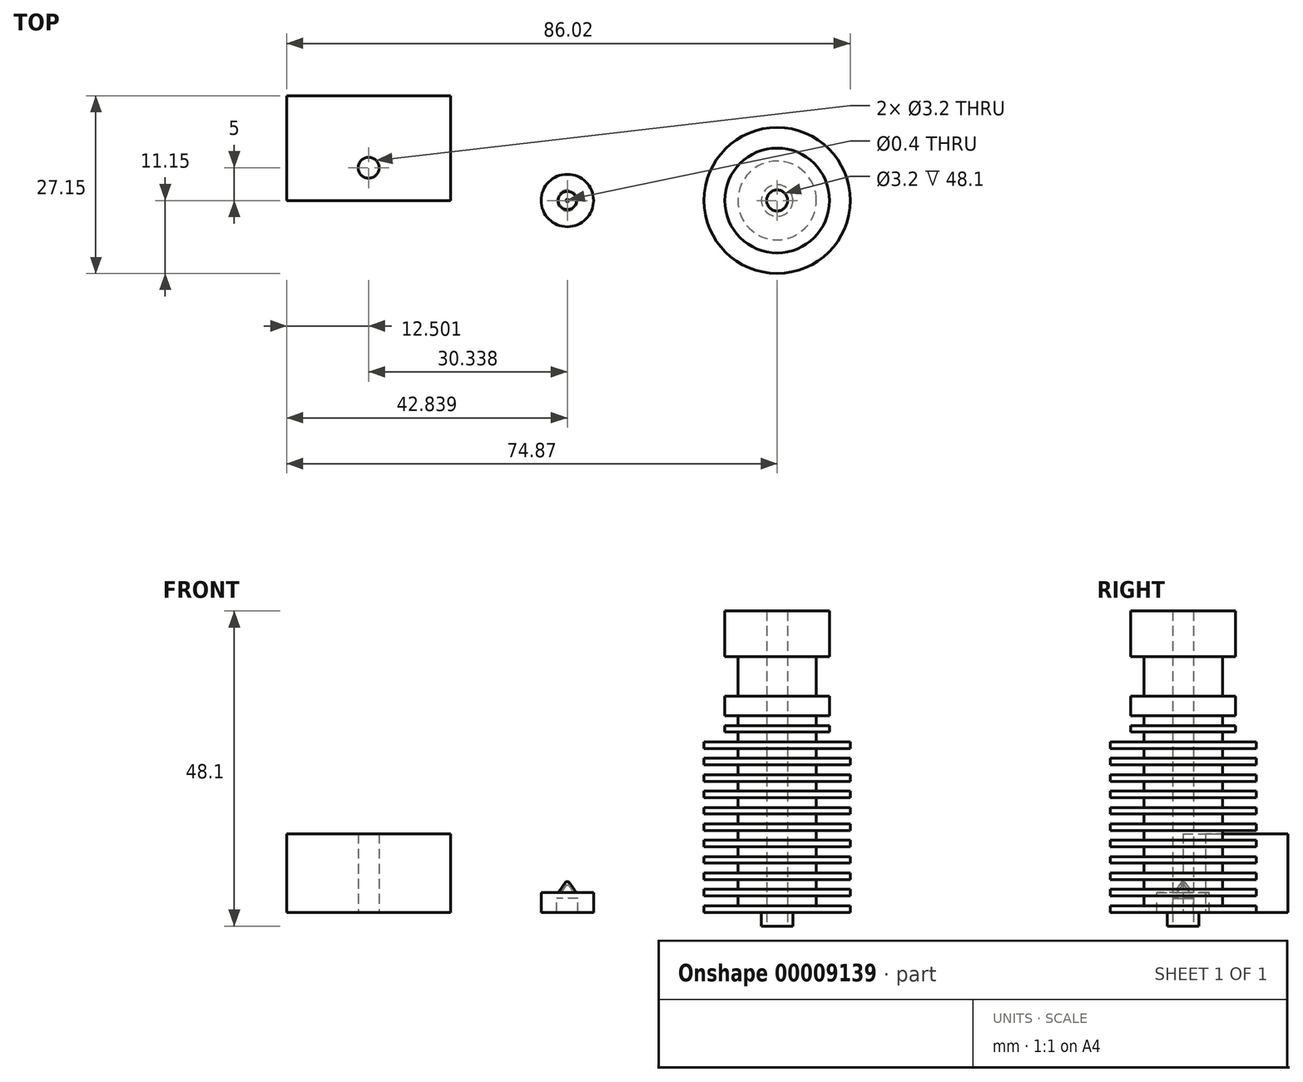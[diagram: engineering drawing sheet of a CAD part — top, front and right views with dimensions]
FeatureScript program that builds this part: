
annotation { "Feature Type Name" : "Feature", "Feature Type Description" : "" }
export const myFeature = defineFeature(function(context is Context, id is Id, definition is map)
    precondition{}
    {
        {
            var Q0;
            Q0=qCreatedBy(makeId("Front.planeOp"),FACE);
            var sketch = newSketch(context, id + "F0", { "sketchPlane" : qUnion([Q0])});
            skLineSegment(sketch, "E0", {"start": v(-11.15, 0) * mm, "end": v(-11.15, 1) * mm});
            skLineSegment(sketch, "E1", {"start": v(-11.15, 1) * mm, "end": v(-6, 1) * mm});
            skLineSegment(sketch, "E2", {"start": v(-6, 1) * mm, "end": v(-6, 2.5) * mm});
            skLineSegment(sketch, "E3", {"start": v(-6, 2.5) * mm, "end": v(-11.15, 2.5) * mm});
            skLineSegment(sketch, "E4", {"start": v(-11.15, 2.5) * mm, "end": v(-11.15, 3.5) * mm});
            skLineSegment(sketch, "E5", {"start": v(-11.15, 3.5) * mm, "end": v(-6, 3.5) * mm});
            skLineSegment(sketch, "E6", {"start": v(-6, 3.5) * mm, "end": v(-6, 5) * mm});
            skLineSegment(sketch, "E7", {"start": v(-6, 5) * mm, "end": v(-11.15, 5) * mm});
            skLineSegment(sketch, "E8", {"start": v(-11.15, 5) * mm, "end": v(-11.15, 6) * mm});
            skLineSegment(sketch, "E9", {"start": v(-11.15, 6) * mm, "end": v(-6, 6) * mm});
            skLineSegment(sketch, "E10", {"start": v(-6, 6) * mm, "end": v(-6, 7.5) * mm});
            skLineSegment(sketch, "E11", {"start": v(-6, 7.5) * mm, "end": v(-11.15, 7.5) * mm});
            skLineSegment(sketch, "E12", {"start": v(-11.15, 7.5) * mm, "end": v(-11.15, 8.5) * mm});
            skLineSegment(sketch, "E13", {"start": v(-11.15, 8.5) * mm, "end": v(-6, 8.5) * mm});
            skLineSegment(sketch, "E14", {"start": v(-6, 8.5) * mm, "end": v(-6, 10) * mm});
            skLineSegment(sketch, "E15", {"start": v(-6, 10) * mm, "end": v(-11.15, 10) * mm});
            skLineSegment(sketch, "E16", {"start": v(-11.15, 10) * mm, "end": v(-11.15, 11) * mm});
            skLineSegment(sketch, "E17", {"start": v(-11.15, 11) * mm, "end": v(-6, 11) * mm});
            skLineSegment(sketch, "E18", {"start": v(-6, 11) * mm, "end": v(-6, 12.5) * mm});
            skLineSegment(sketch, "E19", {"start": v(-6, 12.5) * mm, "end": v(-11.15, 12.5) * mm});
            skLineSegment(sketch, "E20", {"start": v(-11.15, 12.5) * mm, "end": v(-11.15, 13.5) * mm});
            skLineSegment(sketch, "E21", {"start": v(-11.15, 13.5) * mm, "end": v(-6, 13.5) * mm});
            skLineSegment(sketch, "E22", {"start": v(-6, 13.5) * mm, "end": v(-6, 15) * mm});
            skLineSegment(sketch, "E23", {"start": v(-6, 15) * mm, "end": v(-11.15, 15) * mm});
            skLineSegment(sketch, "E24", {"start": v(-11.15, 15) * mm, "end": v(-11.15, 16) * mm});
            skLineSegment(sketch, "E25", {"start": v(-11.15, 16) * mm, "end": v(-6, 16) * mm});
            skLineSegment(sketch, "E26", {"start": v(-6, 16) * mm, "end": v(-6, 17.5) * mm});
            skLineSegment(sketch, "E27", {"start": v(-6, 17.5) * mm, "end": v(-11.15, 17.5) * mm});
            skLineSegment(sketch, "E28", {"start": v(-11.15, 17.5) * mm, "end": v(-11.15, 18.5) * mm});
            skLineSegment(sketch, "E29", {"start": v(-11.15, 18.5) * mm, "end": v(-6, 18.5) * mm});
            skLineSegment(sketch, "E30", {"start": v(-6, 18.5) * mm, "end": v(-6, 20) * mm});
            skLineSegment(sketch, "E31", {"start": v(-6, 20) * mm, "end": v(-11.15, 20) * mm});
            skLineSegment(sketch, "E32", {"start": v(-11.15, 20) * mm, "end": v(-11.15, 21) * mm});
            skLineSegment(sketch, "E33", {"start": v(-11.15, 21) * mm, "end": v(-6, 21) * mm});
            skLineSegment(sketch, "E34", {"start": v(-6, 21) * mm, "end": v(-6, 22.5) * mm});
            skLineSegment(sketch, "E35", {"start": v(-6, 22.5) * mm, "end": v(-11.15, 22.5) * mm});
            skLineSegment(sketch, "E36", {"start": v(-11.15, 22.5) * mm, "end": v(-11.15, 23.5) * mm});
            skLineSegment(sketch, "E37", {"start": v(-11.15, 23.5) * mm, "end": v(-6, 23.5) * mm});
            skLineSegment(sketch, "E38", {"start": v(-6, 23.5) * mm, "end": v(-6, 25) * mm});
            skLineSegment(sketch, "E39", {"start": v(-6, 25) * mm, "end": v(-11.15, 25) * mm});
            skLineSegment(sketch, "E40", {"start": v(-11.15, 25) * mm, "end": v(-11.15, 26) * mm});
            skLineSegment(sketch, "E41", {"start": v(-6, 26) * mm, "end": v(-6, 27.5) * mm});
            skLineSegment(sketch, "E42", {"start": v(-6, 27.5) * mm, "end": v(-8, 27.5) * mm});
            skLineSegment(sketch, "E43", {"start": v(-8, 27.5) * mm, "end": v(-8, 28.5) * mm});
            skLineSegment(sketch, "E44", {"start": v(-8, 28.5) * mm, "end": v(-6, 28.5) * mm});
            skLineSegment(sketch, "E45", {"start": v(-6, 28.5) * mm, "end": v(-6, 30) * mm});
            skLineSegment(sketch, "E46", {"start": v(-6, 30) * mm, "end": v(-8, 30) * mm});
            skLineSegment(sketch, "E47", {"start": v(-8, 30) * mm, "end": v(-8, 33) * mm});
            skLineSegment(sketch, "E48", {"start": v(-11.15, 26) * mm, "end": v(-6, 26) * mm});
            skLineSegment(sketch, "E49", {"start": v(0, 0) * mm, "end": v(0, 46) * mm, "construction": true});
            skLineSegment(sketch, "E50", {"start": v(-8, 33) * mm, "end": v(-6, 33) * mm});
            skLineSegment(sketch, "E51", {"start": v(-6, 33) * mm, "end": v(-6, 39) * mm});
            skLineSegment(sketch, "E52", {"start": v(-6, 39) * mm, "end": v(-8, 39) * mm});
            skLineSegment(sketch, "E53", {"start": v(-8, 39) * mm, "end": v(-8, 46) * mm});
            skLineSegment(sketch, "E54", {"start": v(-8, 46) * mm, "end": v(0, 46) * mm});
            skLineSegment(sketch, "E55", {"start": v(-6, 26) * mm, "end": v(0, 26) * mm, "construction": true});
            skLineSegment(sketch, "E56", {"start": v(-1.6, 46) * mm, "end": v(-1.6, 0) * mm});
            skLineSegment(sketch, "E57", {"start": v(-1.6, 0) * mm, "end": v(-1.6, -2.1) * mm});
            skLineSegment(sketch, "E58", {"start": v(-1.6, -2.1) * mm, "end": v(-2.4, -2.1) * mm});
            skLineSegment(sketch, "E59", {"start": v(-2.4, -2.1) * mm, "end": v(-2.4, 0) * mm});
            skLineSegment(sketch, "E60.trimOffspring", {"start": v(-2.4, 0) * mm, "end": v(-11.15, 0) * mm});
            skSolve(sketch);
        }
        {
            var Q0;
            {var subQ0=sQuery(id+"F0.wireOp",EDGE,"E0");Q0=makeQuery(id+"F0.imprint","IMPRINT",FACE,{"disambiguationData":[TD([[makeQuery(id+"F0.imprint","IMPRINT",EDGE,{"derivedFrom":subQ0}),-1.0]])]});}
            var Q1;
            Q1=sQuery(id+"F0.wireOp",EDGE,"E49");
            revolve(context, id + "F1", {"entities" : qUnion([Q0]), "axis" : qUnion([Q1]), "revolveType" : RevolveType.FULL});
        }
        {
            var Q0;
            Q0=qCreatedBy(makeId("Top.planeOp"),FACE);
            var sketch = newSketch(context, id + "F2", { "sketchPlane" : qUnion([Q0])});
            skLineSegment(sketch, "E61.bottom", {"start": v(-74.87, 0) * mm, "end": v(-49.87, 0) * mm});
            skLineSegment(sketch, "E61.top", {"start": v(-74.87, 16) * mm, "end": v(-49.87, 16) * mm});
            skLineSegment(sketch, "E61.left", {"start": v(-74.87, 0) * mm, "end": v(-74.87, 16) * mm});
            skLineSegment(sketch, "E61.right", {"start": v(-49.87, 0) * mm, "end": v(-49.87, 16) * mm});
            skCircle(sketch, "E62", {"center": v(-62.37, 5) * mm, "radius": 1.6 * mm});
            skLineSegment(sketch, "E63", {"start": v(-62.37, 0) * mm, "end": v(-62.37, 16) * mm, "construction": true});
            skSolve(sketch);
        }
        {
            var Q0;
            Q0=makeQuery(id+"F2.imprint","IMPRINT",FACE,{"disambiguationData":[TD([[makeQuery(id+"F2.imprint","IMPRINT",EDGE,{"derivedFrom":sQuery(id+"F2.wireOp",EDGE,"E61.bottom")}),1.0]])]});
            extrude(context, id + "F3", {"entities" : qUnion([Q0]), "depth" : 12 * mm});
        }
        {
            var Q0;
            Q0=qCreatedBy(makeId("Front.planeOp"),FACE);
            var sketch = newSketch(context, id + "F4", { "sketchPlane" : qUnion([Q0])});
            skLineSegment(sketch, "E64", {"start": v(-33.63, 0) * mm, "end": v(-36.03, 0) * mm});
            skLineSegment(sketch, "E65", {"start": v(-36.03, 0) * mm, "end": v(-36.03, 3) * mm});
            skLineSegment(sketch, "E66", {"start": v(-36.03, 3) * mm, "end": v(-33.42, 3) * mm});
            skLineSegment(sketch, "E67", {"start": v(-33.42, 3) * mm, "end": v(-32.23, 4.7) * mm});
            skLineSegment(sketch, "E68", {"start": v(-32.23, 4.7) * mm, "end": v(-32.23, 4.1) * mm});
            skLineSegment(sketch, "E69", {"start": v(-33.63, 0) * mm, "end": v(-33.63, 2.1) * mm});
            skLineSegment(sketch, "E70", {"start": v(-33.63, 2.1) * mm, "end": v(-32.23, 4.1) * mm});
            skLineSegment(sketch, "E71", {"start": v(-32.03, 7) * mm, "end": v(-32.03, -0.35) * mm, "construction": true});
            skSolve(sketch);
        }
        {
            var Q0;
            Q0=makeQuery(id+"F4.imprint","IMPRINT",FACE,{"disambiguationData":[TD([[makeQuery(id+"F4.imprint","IMPRINT",EDGE,{"derivedFrom":sQuery(id+"F4.wireOp",EDGE,"E64")}),-1.0]])]});
            var Q1;
            Q1=sQuery(id+"F4.wireOp",EDGE,"E71");
            revolve(context, id + "F5", {"entities" : qUnion([Q0]), "axis" : qUnion([Q1]), "revolveType" : RevolveType.FULL});
        }
    });
